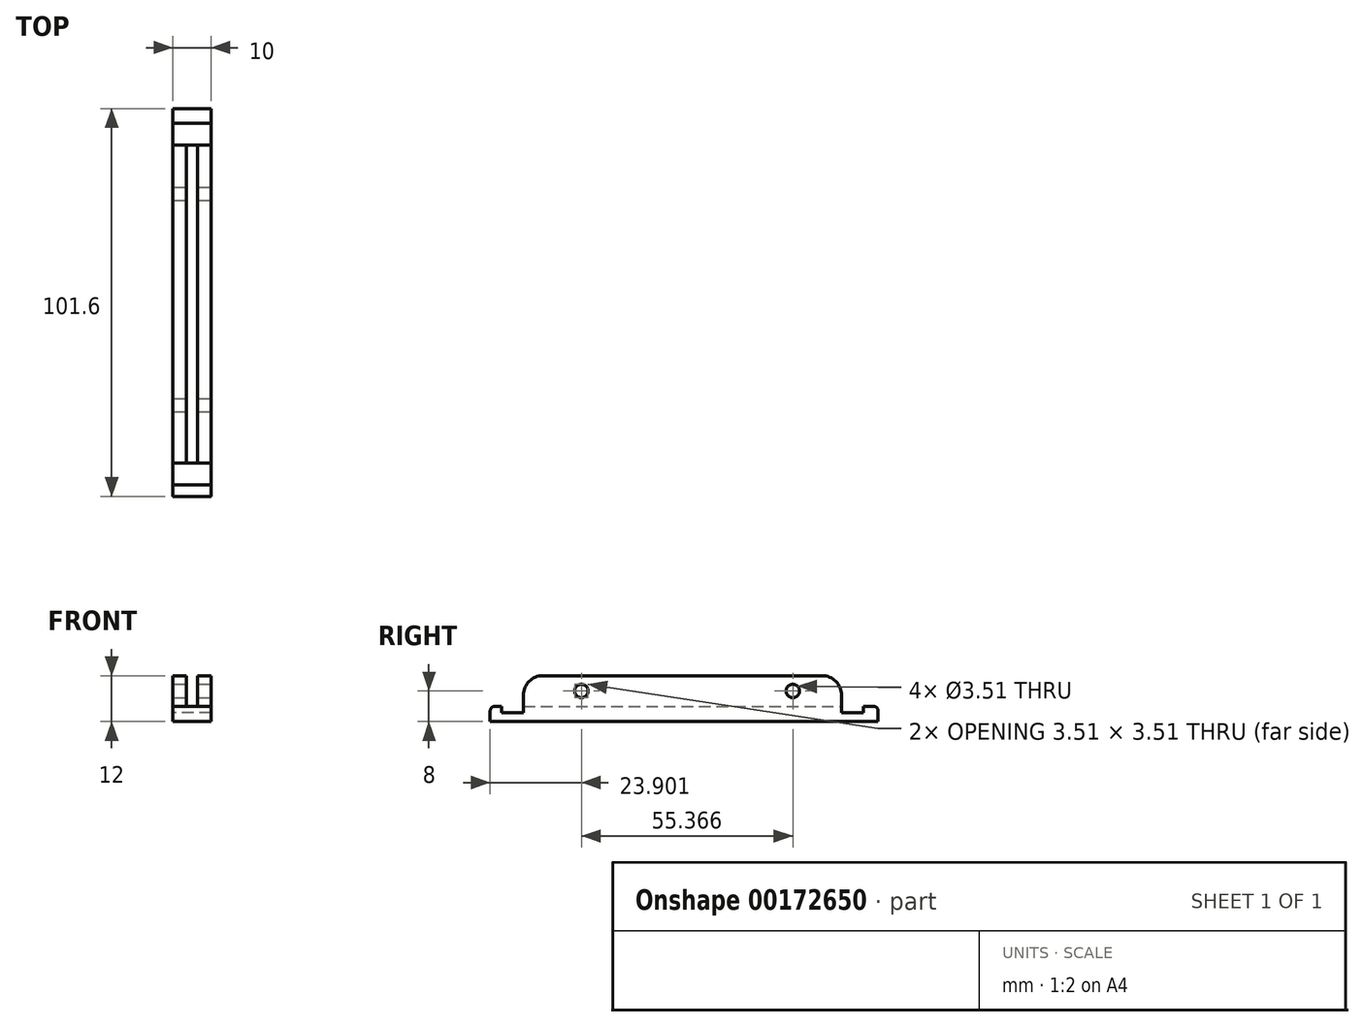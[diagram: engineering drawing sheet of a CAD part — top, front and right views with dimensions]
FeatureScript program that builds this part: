
annotation { "Feature Type Name" : "Feature", "Feature Type Description" : "" }
export const myFeature = defineFeature(function(context is Context, id is Id, definition is map)
    precondition{}
    {
        {
            var Q0;
            Q0=qCreatedBy(makeId("Top.planeOp"),FACE);
            var sketch = newSketch(context, id + "F0", { "sketchPlane" : qUnion([Q0])});
            skLineSegment(sketch, "E0.bottom", {"start": v(-5.96, 65.52) * mm, "end": v(4.04, 65.52) * mm});
            skLineSegment(sketch, "E0.top", {"start": v(-5.96, -36.08) * mm, "end": v(4.04, -36.08) * mm});
            skLineSegment(sketch, "E0.left", {"start": v(-5.96, 65.52) * mm, "end": v(-5.96, -36.08) * mm});
            skLineSegment(sketch, "E0.right", {"start": v(4.04, 65.52) * mm, "end": v(4.04, -36.08) * mm});
            skSolve(sketch);
        }
        {
            var Q0;
            Q0 = qSketchRegion(id + "F0", true);
            extrude(context, id + "F1", {"entities" : qUnion([Q0]), "depth" : 4 * mm});
        }
        {
            var Q0;
            Q0=makeQuery(id+"F1.opExtrude","CAP_FACE",FACE,{"disambiguationData":[OSD([sQuery(id+"F0.wireOp",EDGE,"E0.bottom"),sQuery(id+"F0.wireOp",EDGE,"E0.top"),sQuery(id+"F0.wireOp",EDGE,"E0.left"),sQuery(id+"F0.wireOp",EDGE,"E0.right")])],"isStart":false});
            var sketch = newSketch(context, id + "F2", { "sketchPlane" : qUnion([Q0])});
            skLineSegment(sketch, "E1", {"start": v(4.04, -27.36) * mm, "end": v(4.04, 55.92) * mm});
            skLineSegment(sketch, "E2", {"start": v(0.5, -27.36) * mm, "end": v(0.5, 55.92) * mm});
            skLineSegment(sketch, "E3", {"start": v(0.5, 55.92) * mm, "end": v(4.04, 55.92) * mm});
            skLineSegment(sketch, "E4", {"start": v(-2.42, -27.36) * mm, "end": v(-2.42, 55.92) * mm});
            skLineSegment(sketch, "E5", {"start": v(-2.42, 55.92) * mm, "end": v(-5.96, 55.92) * mm});
            skLineSegment(sketch, "E6", {"start": v(-5.96, 55.92) * mm, "end": v(-5.96, -27.36) * mm});
            skLineSegment(sketch, "E7", {"start": v(-5.96, -27.36) * mm, "end": v(-2.42, -27.36) * mm});
            skLineSegment(sketch, "E8.trimOffspring", {"start": v(0.5, -27.36) * mm, "end": v(4.04, -27.36) * mm});
            skSolve(sketch);
        }
        {
            var Q0;
            Q0 = qSketchRegion(id + "F2", true);
            extrude(context, id + "F3", {"entities" : qUnion([Q0]), "operationType" : NewBodyOperationType.ADD, "depth" : 8 * mm});
        }
        {
            var Q0;
            Q0=makeQuery(id+"F1.opExtrude","CAP_FACE",FACE,{"disambiguationData":[OSD([sQuery(id+"F0.wireOp",EDGE,"E0.bottom"),sQuery(id+"F0.wireOp",EDGE,"E0.top"),sQuery(id+"F0.wireOp",EDGE,"E0.left"),sQuery(id+"F0.wireOp",EDGE,"E0.right")])],"isStart":false});
            var sketch = newSketch(context, id + "F4", { "sketchPlane" : qUnion([Q0])});
            skLineSegment(sketch, "E9.bottom", {"start": v(4.04, 55.92) * mm, "end": v(-5.96, 55.92) * mm});
            skLineSegment(sketch, "E9.top", {"start": v(4.04, 61.63) * mm, "end": v(-5.96, 61.63) * mm});
            skLineSegment(sketch, "E9.left", {"start": v(4.04, 55.92) * mm, "end": v(4.04, 61.63) * mm});
            skLineSegment(sketch, "E9.right", {"start": v(-5.96, 55.92) * mm, "end": v(-5.96, 61.63) * mm});
            skLineSegment(sketch, "E10.bottom", {"start": v(4.04, -27.36) * mm, "end": v(-5.96, -27.36) * mm});
            skLineSegment(sketch, "E10.top", {"start": v(4.04, -33.07) * mm, "end": v(-5.96, -33.07) * mm});
            skLineSegment(sketch, "E10.left", {"start": v(4.04, -27.36) * mm, "end": v(4.04, -33.07) * mm});
            skLineSegment(sketch, "E10.right", {"start": v(-5.96, -27.36) * mm, "end": v(-5.96, -33.07) * mm});
            skSolve(sketch);
        }
        {
            var Q0;
            Q0 = qSketchRegion(id + "F4", true);
            extrude(context, id + "F5", {"entities" : qUnion([Q0]), "operationType" : NewBodyOperationType.REMOVE, "oppositeDirection" : true, "depth" : 1.68 * mm});
        }
        {
            var Q0;
            Q0 = qSketchRegion(id + "F4", true);
            extrude(context, id + "F6", {"entities" : qUnion([Q0]), "operationType" : NewBodyOperationType.REMOVE, "oppositeDirection" : true, "depth" : 1.68 * mm});
        }
        {
            var Q0;
            Q0=makeQuery(id+"F3.boolean.opBoolean","MERGE",FACE,{"derivedFrom":[makeQuery(id+"F1.opExtrude","SWEPT_FACE",FACE,{"disambiguationData":[OSD([sQuery(id+"F0.wireOp",EDGE,"E0.right")])]}),makeQuery(id+"F3.opExtrude","SWEPT_FACE",FACE,{"disambiguationData":[OSD([sQuery(id+"F2.wireOp",EDGE,"E1")])]})]});
            var sketch = newSketch(context, id + "F7", { "sketchPlane" : qUnion([Q0])});
            skCircle(sketch, "E11", {"center": v(-12.18, 8) * mm, "radius": 1.75 * mm});
            skCircle(sketch, "E12", {"center": v(43.19, 8) * mm, "radius": 1.75 * mm});
            skSolve(sketch);
        }
        {
            var Q0;
            Q0 = qSketchRegion(id + "F7", true);
            extrude(context, id + "F8", {"entities" : qUnion([Q0]), "operationType" : NewBodyOperationType.REMOVE, "oppositeDirection" : true, "depth" : 25.4 * mm});
        }
        {
            var Q0;
            Q0=makeQuery(id+"F3.opExtrude","CAP_EDGE",EDGE,{"disambiguationData":[OSD([sQuery(id+"F2.wireOp",EDGE,"E7")])],"isStart":false});
            fillet(context, id + "F9", {"entities" : qUnion([Q0]), "radius" : 5.08 * mm, "tangentPropagation" : true, "allowEdgeOverflow" : false});
        }
        {
            var Q0;
            Q0=makeQuery(id+"F3.opExtrude","CAP_EDGE",EDGE,{"disambiguationData":[OSD([sQuery(id+"F2.wireOp",EDGE,"E8.trimOffspring")])],"isStart":false});
            fillet(context, id + "F10", {"entities" : qUnion([Q0]), "radius" : 5.08 * mm, "tangentPropagation" : true, "allowEdgeOverflow" : false});
        }
        {
            var Q0;
            Q0=makeQuery(id+"F1.opExtrude","CAP_EDGE",EDGE,{"disambiguationData":[OSD([sQuery(id+"F0.wireOp",EDGE,"E0.top")])],"isStart":false});
            fillet(context, id + "F11", {"entities" : qUnion([Q0]), "radius" : 1.27 * mm, "tangentPropagation" : true, "allowEdgeOverflow" : false});
        }
        {
            var Q0;
            Q0=makeQuery(id+"F3.opExtrude","CAP_EDGE",EDGE,{"disambiguationData":[OSD([sQuery(id+"F2.wireOp",EDGE,"E3")])],"isStart":false});
            fillet(context, id + "F12", {"entities" : qUnion([Q0]), "radius" : 5.08 * mm, "tangentPropagation" : true, "allowEdgeOverflow" : false});
        }
        {
            var Q0;
            Q0=makeQuery(id+"F3.opExtrude","CAP_EDGE",EDGE,{"disambiguationData":[OSD([sQuery(id+"F2.wireOp",EDGE,"E5")])],"isStart":false});
            fillet(context, id + "F13", {"entities" : qUnion([Q0]), "radius" : 5.08 * mm, "tangentPropagation" : true, "allowEdgeOverflow" : false});
        }
        {
            var Q0;
            Q0=makeQuery(id+"F1.opExtrude","CAP_EDGE",EDGE,{"disambiguationData":[OSD([sQuery(id+"F0.wireOp",EDGE,"E0.bottom")])],"isStart":false});
            fillet(context, id + "F14", {"entities" : qUnion([Q0]), "radius" : 1.27 * mm, "tangentPropagation" : true, "allowEdgeOverflow" : false});
        }
    });
